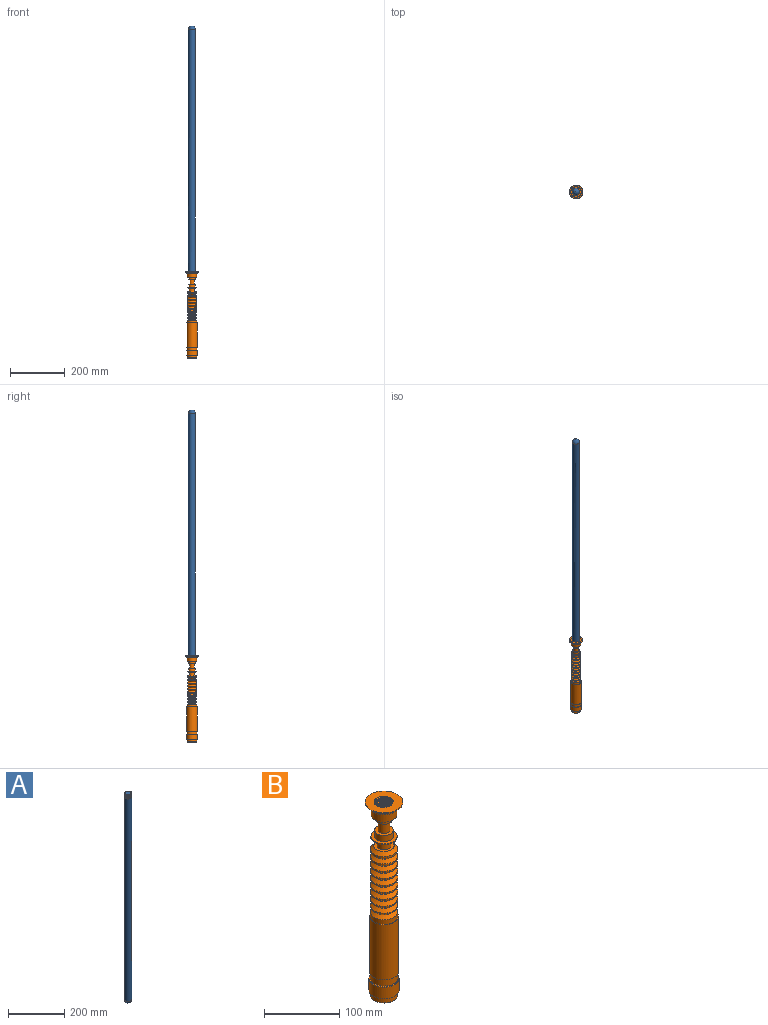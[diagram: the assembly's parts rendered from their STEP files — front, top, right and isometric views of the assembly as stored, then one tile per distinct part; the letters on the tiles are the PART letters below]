
ASSEMBLY  parts=2 mates=1
PART A: 15 faces, bbox 26.3x30.2x916.2 mm
  f0: cylinder r=12.7mm len=886.28mm, axis (0,0,-1), area 70630mm2, adj f9,f11,f12,f13,f14
  f1: cylinder r=12.7mm len=25.4mm, axis (0,0,-1), area 13.4mm2, adj f2,f10,f12,f13
  f2: cylinder r=12.7mm len=25.4mm, axis (0,0,-1), area 23.2mm2, adj f1,f3,f12,f13
  f3: cylinder r=12.7mm len=25.4mm, axis (0,0,-1), area 23.2mm2, adj f2,f4,f12,f13
  f4: cylinder r=12.7mm len=25.4mm, axis (0,0,-1), area 23.2mm2, adj f3,f5,f12,f13
  f5: cylinder r=12.7mm len=25.4mm, axis (0,0,-1), area 23.2mm2, adj f4,f6,f12,f13
  f6: cylinder r=12.7mm len=25.4mm, axis (0,0,-1), area 23.1mm2, adj f5,f7,f12,f13
  f7: cylinder r=12.7mm len=25.4mm, axis (0,0,-1), area 23.1mm2, adj f6,f8,f12,f13
  f8: cylinder r=12.7mm len=25.4mm, axis (0,0,-1), area 23.2mm2, adj f7,f9,f12,f13
  f9: cylinder r=12.7mm len=25.4mm, axis (0,0,-1), area 23.2mm2, adj f0,f8,f12,f13
  f10: plane 25.25x25.24mm, normal (0,0,1), area 464.1mm2, adj f1,f12,f13
  f11: plane 1.53x1.12mm, normal (-0.84,-0.54,0), area 1mm2, adj f0,f12,f13
  f12: bspline ~29.33x25.4mm, area 1090.2mm2, adj f0,f1,f2,f3,f4,f5,f6,f7
  f13: bspline ~29.33x25.4mm, area 1040.3mm2, adj f0,f1,f2,f3,f4,f5,f6,f7
  f14: sphere r=12.7mm, area 1013.4mm2, adj f0
PART B: 67 faces, bbox 51.3x51.3x316.6 mm
  f0: cylinder r=11.91mm len=23.81mm, axis (0,0,1), area 324.6mm2, adj f58,f63,f64,f65,f66
  f1: cylinder r=17.98mm len=35.97mm, axis (0,0,-1), area 861mm2, adj f5,f62
  f2: plane 34.95x34.95mm, normal (0,0,-1), area 959.4mm2, adj f62
  f3: cylinder r=20.04mm len=40.08mm, axis (0,0,-1), area 2379.6mm2, adj f60,f61
  f4: plane 39.07x39.07mm, normal (0,0,1), area 163.9mm2, adj f6,f60
  f5: plane 39.07x39.07mm, normal (0,0,-1), area 182.6mm2, adj f1,f61
  f6: cylinder r=18.15mm len=36.3mm, axis (0,0,-1), area 1216.5mm2, adj f4,f9
  f7: cylinder r=19.16mm len=89.79mm, axis (0,0,-1), area 10811.7mm2, adj f8,f9
  f8: plane 38.33x38.33mm, normal (0,0,1), area 122mm2, adj f7,f10
  f9: plane 38.33x38.33mm, normal (0,0,-1), area 119.1mm2, adj f6,f7
  f10: cylinder r=18.12mm len=36.25mm, axis (0,0,-1), area 838.8mm2, adj f8,f11
  f11: cone r=13.47mm half-angle=45deg, axis (0,0,-1), area 652.5mm2, adj f10,f12
  f12: cone r=18.12mm half-angle=45deg, axis (0,0,1), area 652.5mm2, adj f11,f13
  f13: cylinder r=18.12mm len=36.25mm, axis (0,0,-1), area 173.5mm2, adj f12,f14
  f14: cone r=13.47mm half-angle=45deg, axis (0,0,-1), area 652.5mm2, adj f13,f15
  f15: cone r=18.12mm half-angle=45deg, axis (0,0,1), area 652.5mm2, adj f14,f16
  f16: cylinder r=18.12mm len=36.25mm, axis (0,0,-1), area 208.2mm2, adj f15,f17
  f17: cone r=13.47mm half-angle=45deg, axis (0,0,-1), area 652.5mm2, adj f16,f18
  f18: cone r=18.12mm half-angle=45deg, axis (0,0,1), area 652.5mm2, adj f17,f19
  f19: cylinder r=18.12mm len=36.25mm, axis (0,0,-1), area 240.1mm2, adj f18,f20
  f20: cone r=13.47mm half-angle=45deg, axis (0,0,-1), area 652.5mm2, adj f19,f21
  f21: cone r=18.12mm half-angle=45deg, axis (0,0,1), area 652.5mm2, adj f20,f22
  f22: cylinder r=18.12mm len=36.25mm, axis (0,0,-1), area 231.4mm2, adj f21,f23
  f23: cone r=13.47mm half-angle=45deg, axis (0,0,-1), area 652.5mm2, adj f22,f24
  f24: cone r=18.12mm half-angle=45deg, axis (0,0,1), area 652.5mm2, adj f23,f25
  f25: cylinder r=18.12mm len=36.25mm, axis (0,0,-1), area 237.2mm2, adj f24,f26
  f26: cone r=13.47mm half-angle=45deg, axis (0,0,-1), area 652.5mm2, adj f25,f27
  f27: cone r=18.12mm half-angle=45deg, axis (0,0,1), area 652.5mm2, adj f26,f28
  f28: cylinder r=18.12mm len=36.25mm, axis (0,0,-1), area 240.1mm2, adj f27,f29
  f29: cone r=13.47mm half-angle=45deg, axis (0,0,-1), area 652.5mm2, adj f28,f30
  f30: cone r=18.12mm half-angle=45deg, axis (0,0,1), area 652.5mm2, adj f29,f31
  f31: cylinder r=18.12mm len=36.25mm, axis (0,0,-1), area 248.7mm2, adj f30,f32
  f32: cone r=13.47mm half-angle=45deg, axis (0,0,-1), area 652.5mm2, adj f31,f33
  f33: cone r=18.12mm half-angle=45deg, axis (0,0,1), area 652.5mm2, adj f32,f34
  f34: cylinder r=18.12mm len=36.25mm, axis (0,0,-1), area 283.4mm2, adj f33,f35
  f35: cone r=13.47mm half-angle=45deg, axis (0,0,-1), area 652.5mm2, adj f34,f36
  f36: cone r=18.12mm half-angle=45deg, axis (0,0,1), area 652.5mm2, adj f35,f37
  f37: cylinder r=18.12mm len=36.25mm, axis (0,0,-1), area 318.2mm2, adj f36,f39
  f38: plane 26.95x26.95mm, normal (0,0,1), area 308.5mm2, adj f39,f40
  f39: cone r=13.47mm half-angle=45deg, axis (0,0,-1), area 652.5mm2, adj f37,f38
  f40: cylinder r=9.13mm len=18.26mm, axis (0,0,-1), area 676.2mm2, adj f38,f42
  f41: cylinder r=11.06mm len=22.12mm, axis (0,0,-1), area 141.2mm2, adj f42,f45
  f42: plane 22.12x22.12mm, normal (0,0,-1), area 122.5mm2, adj f40,f41
  f43: cylinder r=17.44mm len=34.87mm, axis (0,0,-1), area 194.8mm2, adj f44,f45
  f44: plane 34.87x34.87mm, normal (0,0,1), area 469.2mm2, adj f43,f46
  f45: plane 34.87x34.87mm, normal (0,0,-1), area 570.8mm2, adj f41,f43
  f46: cylinder r=12.44mm len=24.87mm, axis (0,0,-1), area 774.1mm2, adj f44,f47
  f47: plane 24.87x24.87mm, normal (0,0,1), area 289.3mm2, adj f46,f48
  f48: cylinder r=7.91mm len=17.45mm, axis (0,0,-1), area 867.5mm2, adj f47,f50
  f49: cylinder r=11.23mm len=22.45mm, axis (0,0,-1), area 519.6mm2, adj f50,f52
  f50: plane 22.45x22.45mm, normal (0,0,-1), area 199.3mm2, adj f48,f49
  f51: cylinder r=16.89mm len=33.78mm, axis (0,0,-1), area 1401.8mm2, adj f52,f54
  f52: plane 33.78x33.78mm, normal (0,0,-1), area 500.3mm2, adj f49,f51
  f53: cylinder r=18.91mm len=37.82mm, axis (0,0,-1), area 362.2mm2, adj f54,f56
  f54: plane 37.82x37.82mm, normal (0,0,-1), area 227.1mm2, adj f51,f53
  f55: cylinder r=19.52mm len=39.04mm, axis (0,0,-1), area 451.7mm2, adj f56,f59
  f56: plane 39.04x39.04mm, normal (0,0,-1), area 73.6mm2, adj f53,f55
  f57: cylinder r=25.16mm len=50.32mm, axis (0,0,-1), area 172.7mm2, adj f58,f59
  f58: plane 51.29x51.29mm, normal (0,0,1), area 1500.2mm2, adj f0,f57,f65,f66
  f59: plane 50.32x50.32mm, normal (0,0,-1), area 791.5mm2, adj f55,f57
  f60: cone r=19.53mm half-angle=45deg, axis (0,0,-1), area 89.3mm2, adj f3,f4
  f61: cone r=20.04mm half-angle=45deg, axis (0,0,1), area 89.3mm2, adj f3,f5
  f62: cone r=17.98mm half-angle=45deg, axis (0,0,1), area 80mm2, adj f1,f2
  f63: plane 23.81x23.81mm, normal (0,0,1), area 445.3mm2, adj f0
  f64: plane 1.52x1.32mm, normal (0,1,0), area 1mm2, adj f0,f65,f66
  f65: bspline ~30.54x26.45mm, area 1156.1mm2, adj f0,f58,f64,f66
  f66: bspline ~30.54x26.45mm, area 1107.4mm2, adj f0,f58,f64,f65
PLACE A rot(axis=(1,0,0),180deg) t=(-91.63,6.72,1275.94)mm
PLACE B t=(-91.11,6.44,64.64)mm
MATE fastened A.f10 <-> B.f0  axis (0,0,-1) through (-91.11,6.44,361.54)mm
